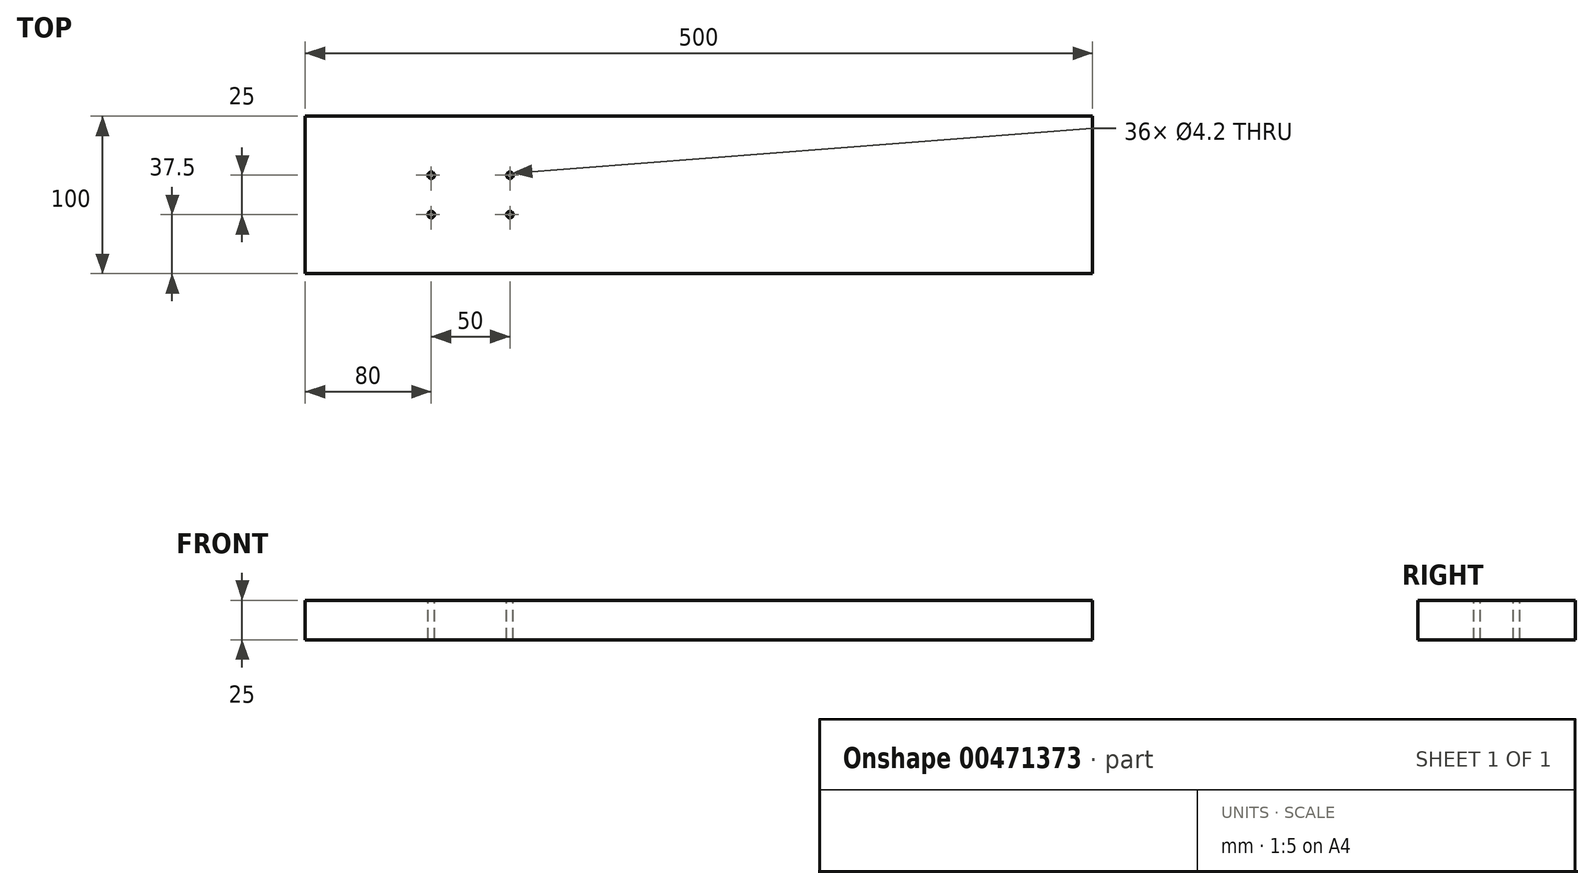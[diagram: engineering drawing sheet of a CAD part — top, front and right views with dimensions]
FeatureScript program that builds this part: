
annotation { "Feature Type Name" : "Feature", "Feature Type Description" : "" }
export const myFeature = defineFeature(function(context is Context, id is Id, definition is map)
    precondition{}
    {
        {
            var Q0;
            Q0=qCreatedBy(makeId("Top.planeOp"),FACE);
            var sketch = newSketch(context, id + "F0", { "sketchPlane" : qUnion([Q0])});
            skLineSegment(sketch, "E0.bottom", {"start": v(-250, 50) * mm, "end": v(250, 50) * mm});
            skLineSegment(sketch, "E0.top", {"start": v(-250, -50) * mm, "end": v(250, -50) * mm});
            skLineSegment(sketch, "E0.left", {"start": v(-250, 50) * mm, "end": v(-250, -50) * mm});
            skLineSegment(sketch, "E0.right", {"start": v(250, 50) * mm, "end": v(250, -50) * mm});
            skPoint(sketch, "E0.middle", {"position": v(0, 0) * mm});
            skSolve(sketch);
        }
        {
            var Q0;
            Q0 = qSketchRegion(id + "F0", true);
            extrude(context, id + "F1", {"entities" : qUnion([Q0]), "depth" : 25 * mm});
        }
        {
            var Q0;
            Q0=makeQuery(id+"F1.opExtrude","CAP_FACE",FACE,{"disambiguationData":[OSD([sQuery(id+"F0.wireOp",EDGE,"E0.bottom"),sQuery(id+"F0.wireOp",EDGE,"E0.top"),sQuery(id+"F0.wireOp",EDGE,"E0.left"),sQuery(id+"F0.wireOp",EDGE,"E0.right")])],"isStart":false});
            var sketch = newSketch(context, id + "F2", { "sketchPlane" : qUnion([Q0])});
            skPoint(sketch, "E1", {"position": v(-170, 12.5) * mm});
            skPoint(sketch, "E2", {"position": v(-170, -12.5) * mm});
            skPoint(sketch, "E3", {"position": v(-120, 12.5) * mm});
            skPoint(sketch, "E4", {"position": v(-120, -12.5) * mm});
            skLineSegment(sketch, "E5", {"start": v(-170, 12.5) * mm, "end": v(-120, 12.5) * mm, "construction": true});
            skLineSegment(sketch, "E6", {"start": v(-120, 12.5) * mm, "end": v(-120, -12.5) * mm, "construction": true});
            skLineSegment(sketch, "E7", {"start": v(-170, -12.5) * mm, "end": v(-120, -12.5) * mm, "construction": true});
            skLineSegment(sketch, "E8", {"start": v(-170, 12.5) * mm, "end": v(-170, -12.5) * mm, "construction": true});
            skLineSegment(sketch, "E9", {"start": v(-170, 12.5) * mm, "end": v(-120, -12.5) * mm, "construction": true});
            skLineSegment(sketch, "E10", {"start": v(0, 0) * mm, "end": v(-145, 0) * mm, "construction": true});
            skSolve(sketch);
        }
        {
            var Q0;
            Q0=sQuery(id+"F2.wireOp",VERTEX,"E1");
            var Q1;
            Q1=sQuery(id+"F2.wireOp",VERTEX,"E3");
            var Q2;
            Q2=sQuery(id+"F2.wireOp",VERTEX,"E4");
            var Q3;
            Q3=sQuery(id+"F2.wireOp",VERTEX,"E2");
            var Q4;
            Q4=makeQuery(id+"F1.opExtrude","SWEPT_BODY",BODY,{"disambiguationData":[OSD([sQuery(id+"F0.wireOp",EDGE,"E0.bottom"),sQuery(id+"F0.wireOp",EDGE,"E0.top"),sQuery(id+"F0.wireOp",EDGE,"E0.left"),sQuery(id+"F0.wireOp",EDGE,"E0.right")])]});
            hole(context, id + "F3", {"style" : HoleStyle.SIMPLE, "endStyle" : HoleEndStyle.THROUGH, "standardTappedOrClearance" : lookupTablePath({ "standard" : "ISO", "engagement" : "75%", "pitch" : "0.8 mm", "size" : "M5", "type" : "Tapped" }), "standardBlindInLast" : lookupTablePath({ "standard" : "ISO", "engagement" : "75%", "pitch" : "0.8 mm", "size" : "M5", "type" : "Tapped" }), "holeDiameter" : 4.2 * mm, "showTappedDepth" : true, "isTappedThrough" : true, "tappedDepth" : 12 * mm, "tapClearance" : 3, "locations" : qUnion([Q0, Q1, Q2, Q3]), "scope" : qUnion([Q4]), "majorDiameter" : 5 * mm});
        }
    });
